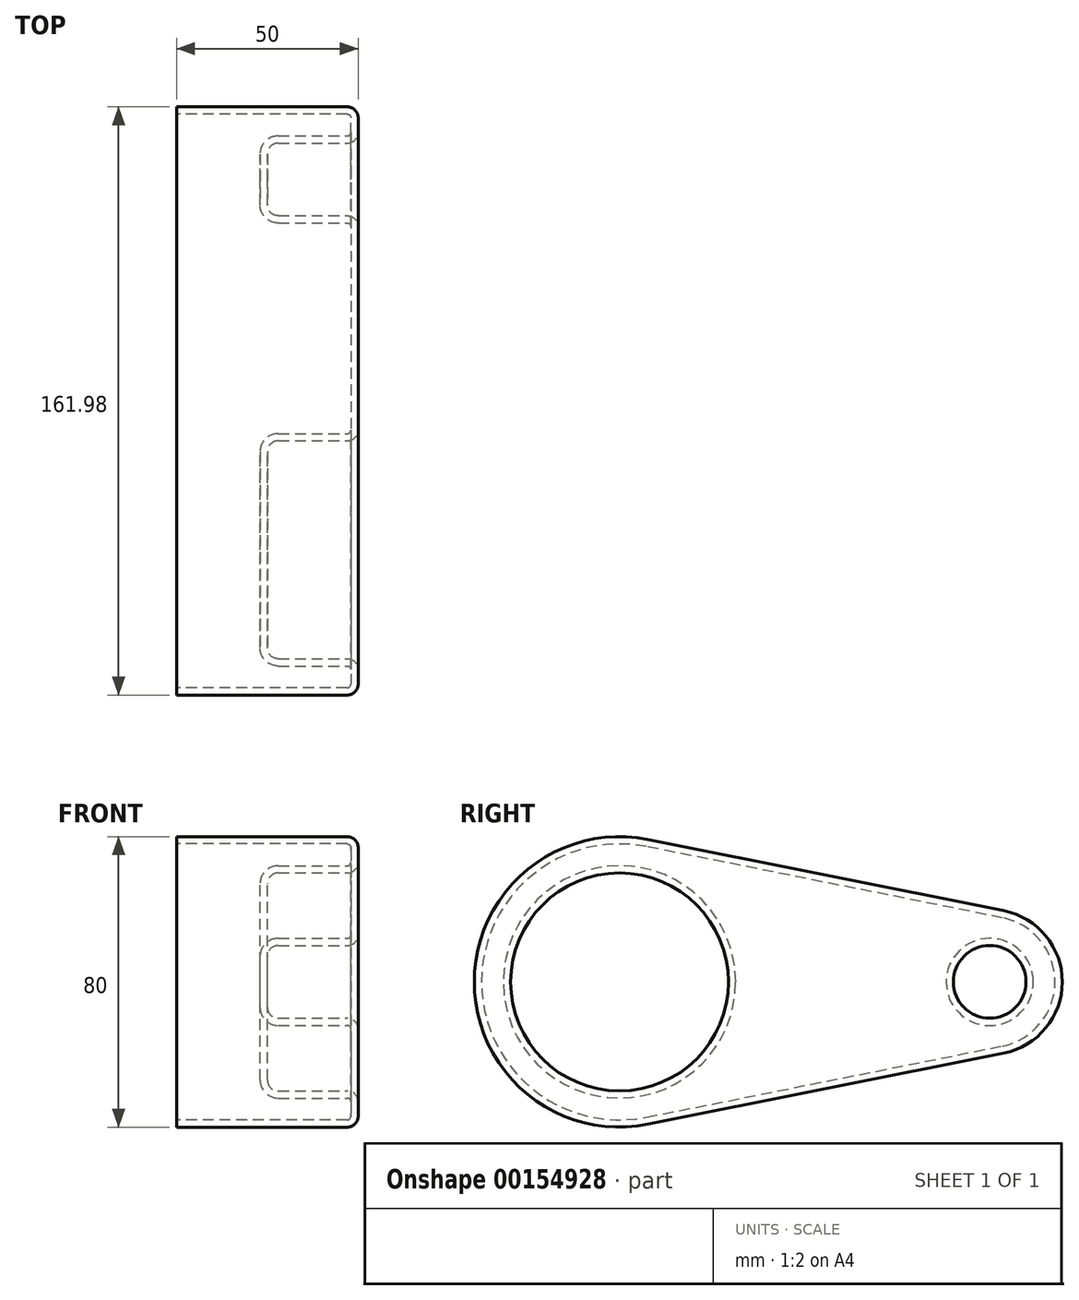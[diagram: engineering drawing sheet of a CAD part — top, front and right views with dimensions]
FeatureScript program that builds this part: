
annotation { "Feature Type Name" : "Feature", "Feature Type Description" : "" }
export const myFeature = defineFeature(function(context is Context, id is Id, definition is map)
    precondition{}
    {
        {
            var Q0;
            Q0=qCreatedBy(makeId("Right.planeOp"),FACE);
            var sketch = newSketch(context, id + "F0", { "sketchPlane" : qUnion([Q0])});
            skCircle(sketch, "E0", {"center": v(0, 0) * mm, "radius": 40 * mm});
            skCircle(sketch, "E1", {"center": v(101.98, 0) * mm, "radius": 20 * mm});
            skLineSegment(sketch, "E2", {"start": v(105.9, 19.61) * mm, "end": v(7.84, 39.22) * mm});
            skLineSegment(sketch, "E3", {"start": v(7.84, -39.22) * mm, "end": v(105.9, -19.61) * mm});
            skSolve(sketch);
        }
        {
            var Q0;
            {var subQ0=sQuery(id+"F0.wireOp",EDGE,"E0");var subQ1=makeQuery(id+"F0.imprint","INTERSECT",VERTEX,{"derivedFrom":[subQ0,sQuery(id+"F0.wireOp",EDGE,"E2")]});Q0=makeQuery(id+"F0.imprint","IMPRINT",FACE,{"disambiguationData":[TD([[makeQuery(id+"F0.imprint","IMPRINT",EDGE,{"disambiguationData":[TD([[subQ1,-1.0]])],"derivedFrom":subQ0}),1.0]])]});}
            var Q1;
            {var subQ0=sQuery(id+"F0.wireOp",EDGE,"E2");Q1=makeQuery(id+"F0.imprint","IMPRINT",FACE,{"disambiguationData":[TD([[makeQuery(id+"F0.imprint","IMPRINT",EDGE,{"derivedFrom":subQ0}),1.0]])]});}
            var Q2;
            {var subQ0=sQuery(id+"F0.wireOp",EDGE,"E1");var subQ1=makeQuery(id+"F0.imprint","INTERSECT",VERTEX,{"derivedFrom":[subQ0,sQuery(id+"F0.wireOp",EDGE,"E2")]});Q2=makeQuery(id+"F0.imprint","IMPRINT",FACE,{"disambiguationData":[TD([[makeQuery(id+"F0.imprint","IMPRINT",EDGE,{"disambiguationData":[TD([[subQ1,-1.0]])],"derivedFrom":subQ0}),1.0]])]});}
            extrude(context, id + "F1", {"entities" : qUnion([Q0, Q1, Q2]), "depth" : 50 * mm});
        }
        {
            var Q0;
            Q0=makeQuery(id+"F1.opExtrude","CAP_FACE",FACE,{"disambiguationData":[OSD([sQuery(id+"F0.wireOp",EDGE,"E0"),sQuery(id+"F0.wireOp",EDGE,"E1"),sQuery(id+"F0.wireOp",EDGE,"E2"),sQuery(id+"F0.wireOp",EDGE,"E3")])],"isStart":false});
            var sketch = newSketch(context, id + "F2", { "sketchPlane" : qUnion([Q0])});
            skCircle(sketch, "E4", {"center": v(0, 0) * mm, "radius": 30 * mm});
            skCircle(sketch, "E5", {"center": v(101.98, 0) * mm, "radius": 10 * mm});
            skSolve(sketch);
        }
        {
            var Q0;
            Q0=makeQuery(id+"F2.imprint","IMPRINT",FACE,{"disambiguationData":[TD([[makeQuery(id+"F2.imprint","IMPRINT",EDGE,{"derivedFrom":sQuery(id+"F2.wireOp",EDGE,"E4")}),1.0]])]});
            var Q1;
            Q1=makeQuery(id+"F2.imprint","IMPRINT",FACE,{"disambiguationData":[TD([[makeQuery(id+"F2.imprint","IMPRINT",EDGE,{"derivedFrom":sQuery(id+"F2.wireOp",EDGE,"E5")}),1.0]])]});
            extrude(context, id + "F3", {"entities" : qUnion([Q0, Q1]), "operationType" : NewBodyOperationType.REMOVE, "oppositeDirection" : true, "depth" : 25 * mm});
        }
        {
            var Q0;
            Q0=makeQuery(id+"F1.opExtrude","CAP_FACE",FACE,{"disambiguationData":[OSD([sQuery(id+"F0.wireOp",EDGE,"E0"),sQuery(id+"F0.wireOp",EDGE,"E1"),sQuery(id+"F0.wireOp",EDGE,"E2"),sQuery(id+"F0.wireOp",EDGE,"E3")])],"isStart":false});
            var Q1;
            Q1=makeQuery(id+"F3.boolean.opBoolean","COPY",FACE,{"derivedFrom":makeQuery(id+"F3.opExtrude","CAP_FACE",FACE,{"disambiguationData":[OSD([sQuery(id+"F2.wireOp",EDGE,"E4")])],"isStart":false})});
            var Q2;
            Q2=makeQuery(id+"F3.boolean.opBoolean","COPY",FACE,{"derivedFrom":makeQuery(id+"F3.opExtrude","CAP_FACE",FACE,{"disambiguationData":[OSD([sQuery(id+"F2.wireOp",EDGE,"E5")])],"isStart":false})});
            fillet(context, id + "F4", {"entities" : qUnion([Q0, Q1, Q2]), "radius" : 3 * mm, "tangentPropagation" : true, "allowEdgeOverflow" : false});
        }
        {
            var Q0;
            Q0=makeQuery(id+"F1.opExtrude","CAP_FACE",FACE,{"disambiguationData":[OSD([sQuery(id+"F0.wireOp",EDGE,"E0"),sQuery(id+"F0.wireOp",EDGE,"E1"),sQuery(id+"F0.wireOp",EDGE,"E2"),sQuery(id+"F0.wireOp",EDGE,"E3")])],"isStart":true});
            var Q1;
            Q1=makeQuery(id+"F1.opExtrude","SWEPT_BODY",BODY,{"disambiguationData":[OSD([sQuery(id+"F0.wireOp",EDGE,"E0"),sQuery(id+"F0.wireOp",EDGE,"E1"),sQuery(id+"F0.wireOp",EDGE,"E2"),sQuery(id+"F0.wireOp",EDGE,"E3")])]});
            shell(context, id + "F5", {"entities" : qUnion([Q0]), "parts" : qUnion([Q1]), "thickness" : 2 * mm});
        }
    });
